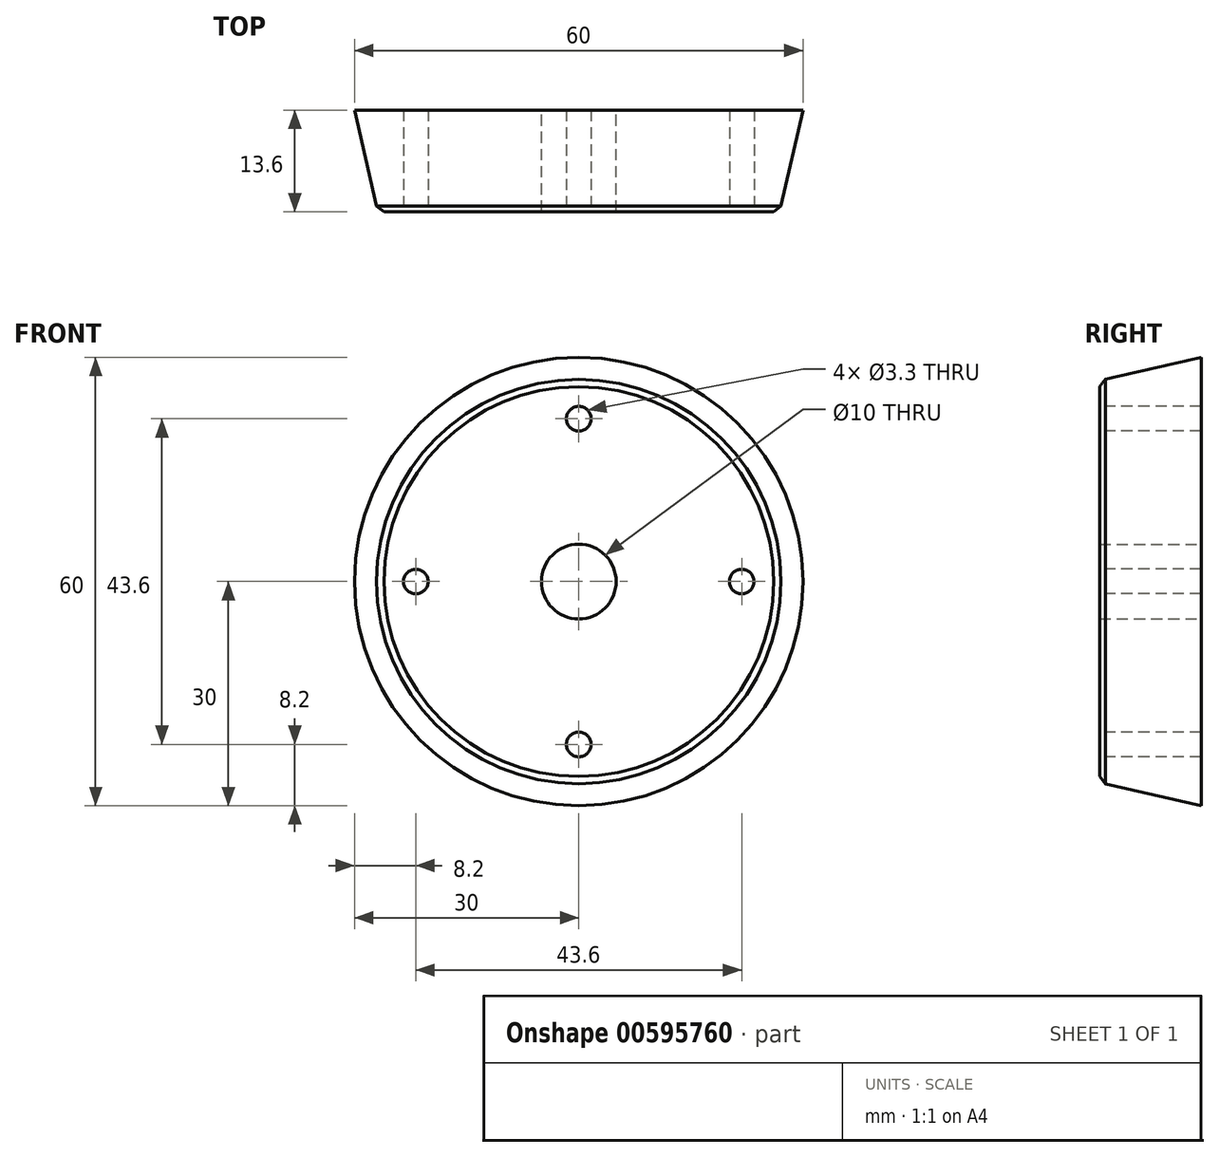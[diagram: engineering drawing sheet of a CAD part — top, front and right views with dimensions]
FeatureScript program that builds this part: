
annotation { "Feature Type Name" : "Feature", "Feature Type Description" : "" }
export const myFeature = defineFeature(function(context is Context, id is Id, definition is map)
    precondition{}
    {
        {
            var Q0;
            Q0=qCreatedBy(makeId("Right.planeOp"),FACE);
            var sketch = newSketch(context, id + "F0", { "sketchPlane" : qUnion([Q0])});
            skLineSegment(sketch, "E0", {"start": v(0, 0) * mm, "end": v(-13.6, 0) * mm});
            skLineSegment(sketch, "E1", {"start": v(-13.6, 0) * mm, "end": v(-13.6, 26.87) * mm});
            skLineSegment(sketch, "E2", {"start": v(-13.6, 26.87) * mm, "end": v(0, 30) * mm});
            skLineSegment(sketch, "E3", {"start": v(0, 30) * mm, "end": v(0, 0) * mm});
            skSolve(sketch);
        }
        {
            var Q0;
            Q0=makeQuery(id+"F0.imprint","IMPRINT",FACE,{"disambiguationData":[TD([[makeQuery(id+"F0.imprint","IMPRINT",EDGE,{"derivedFrom":sQuery(id+"F0.wireOp",EDGE,"E0")}),-1.0]])]});
            var Q1;
            Q1=sQuery(id+"F0.wireOp",EDGE,"E0");
            revolve(context, id + "F1", {"entities" : qUnion([Q0]), "axis" : qUnion([Q1]), "revolveType" : RevolveType.FULL});
        }
        {
            var Q0;
            Q0=makeQuery(id+"F1.opRevolve","SWEPT_FACE",FACE,{"disambiguationData":[OSD([sQuery(id+"F0.wireOp",EDGE,"E3")])]});
            var sketch = newSketch(context, id + "F2", { "sketchPlane" : qUnion([Q0])});
            skPoint(sketch, "E4", {"position": v(0, 0) * mm});
            skSolve(sketch);
        }
        {
            var Q0;
            Q0=sQuery(id+"F2.wireOp",VERTEX,"E4");
            var Q1;
            Q1=makeQuery(id+"F1.opRevolve","SWEPT_BODY",BODY,{"disambiguationData":[OSD([sQuery(id+"F0.wireOp",EDGE,"E0"),sQuery(id+"F0.wireOp",EDGE,"E1"),sQuery(id+"F0.wireOp",EDGE,"E2"),sQuery(id+"F0.wireOp",EDGE,"E3")])]});
            hole(context, id + "F3", {"style" : HoleStyle.SIMPLE, "endStyle" : HoleEndStyle.THROUGH, "holeDiameter" : 10 * mm, "majorDiameter" : 5 * mm, "isTappedThrough" : true, "tappedDepth" : 12 * mm, "tapClearance" : 3, "locations" : qUnion([Q0]), "scope" : qUnion([Q1])});
        }
        {
            var Q0;
            Q0=makeQuery(id+"F1.opRevolve","SWEPT_FACE",FACE,{"disambiguationData":[OSD([sQuery(id+"F0.wireOp",EDGE,"E1")])]});
            var sketch = newSketch(context, id + "F4", { "sketchPlane" : qUnion([Q0])});
            skCircle(sketch, "E5", {"center": v(0, 0) * mm, "radius": 21.8 * mm, "construction": true});
            skLineSegment(sketch, "E6", {"start": v(0, 21.8) * mm, "end": v(0, -21.8) * mm, "construction": true});
            skLineSegment(sketch, "E7", {"start": v(21.8, 0) * mm, "end": v(-21.8, 0) * mm, "construction": true});
            skPoint(sketch, "E8", {"position": v(0, 21.8) * mm});
            skPoint(sketch, "E9", {"position": v(21.8, 0) * mm});
            skPoint(sketch, "E10", {"position": v(0, -21.8) * mm});
            skPoint(sketch, "E11", {"position": v(-21.8, 0) * mm});
            skSolve(sketch);
        }
        {
            var Q0;
            Q0=makeQuery(id+"F1.opRevolve","SWEPT_EDGE",EDGE,{"disambiguationData":[OSD([sQuery(id+"F0.wireOp",EDGE,"E1"),sQuery(id+"F0.wireOp",EDGE,"E2")])]});
            chamfer(context, id + "F5", {"entities" : qUnion([Q0]), "width" : 1 * mm, "tangentPropagation" : true});
        }
        {
            var Q0;
            Q0=sQuery(id+"F4.wireOp",VERTEX,"E8");
            var Q1;
            Q1=sQuery(id+"F4.wireOp",VERTEX,"E9");
            var Q2;
            Q2=sQuery(id+"F4.wireOp",VERTEX,"E10");
            var Q3;
            Q3=sQuery(id+"F4.wireOp",VERTEX,"E11");
            var Q4;
            Q4=makeQuery(id+"F1.opRevolve","SWEPT_BODY",BODY,{"disambiguationData":[OSD([sQuery(id+"F0.wireOp",EDGE,"E0"),sQuery(id+"F0.wireOp",EDGE,"E1"),sQuery(id+"F0.wireOp",EDGE,"E2"),sQuery(id+"F0.wireOp",EDGE,"E3")])]});
            hole(context, id + "F6", {"style" : HoleStyle.SIMPLE, "endStyle" : HoleEndStyle.THROUGH, "standardTappedOrClearance" : lookupTablePath({ "standard" : "ISO", "engagement" : "75%", "pitch" : "0.7 mm", "size" : "M4", "type" : "Tapped" }), "standardBlindInLast" : lookupTablePath({ "standard" : "ISO", "engagement" : "75%", "pitch" : "0.7 mm", "size" : "M4", "type" : "Tapped" }), "holeDiameter" : 3.3 * mm, "majorDiameter" : 4 * mm, "showTappedDepth" : true, "isTappedThrough" : true, "tappedDepth" : 12 * mm, "tapClearance" : 3, "locations" : qUnion([Q0, Q1, Q2, Q3]), "scope" : qUnion([Q4])});
        }
    });
